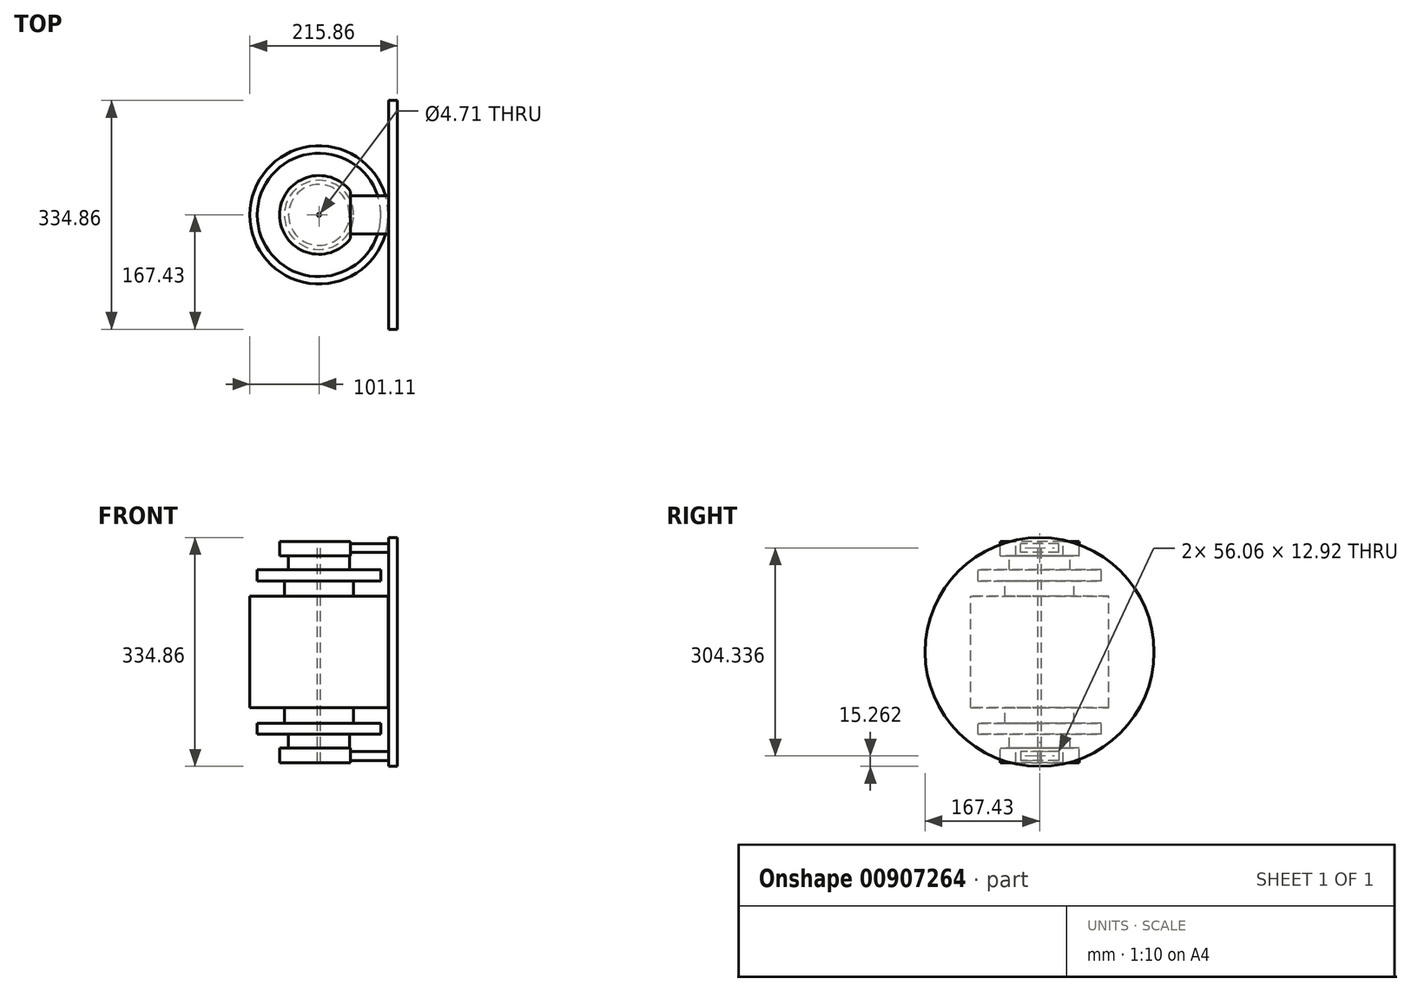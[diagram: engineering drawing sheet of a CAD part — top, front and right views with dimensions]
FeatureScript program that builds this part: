
annotation { "Feature Type Name" : "Feature", "Feature Type Description" : "" }
export const myFeature = defineFeature(function(context is Context, id is Id, definition is map)
    precondition{}
    {
        {
            var Q0;
            Q0=qCreatedBy(makeId("Front.planeOp"),FACE);
            var sketch = newSketch(context, id + "F0", { "sketchPlane" : qUnion([Q0])});
            skLineSegment(sketch, "E0", {"start": v(0, 161.96) * mm, "end": v(0, -142.84) * mm, "construction": true});
            skLineSegment(sketch, "E1", {"start": v(2.35, 161.96) * mm, "end": v(2.35, -142.84) * mm});
            skLineSegment(sketch, "E2", {"start": v(2.35, 161.96) * mm, "end": v(19.28, 161.96) * mm});
            skLineSegment(sketch, "E3", {"start": v(19.28, 161.96) * mm, "end": v(57.62, 161.96) * mm});
            skLineSegment(sketch, "E4", {"start": v(57.62, 161.96) * mm, "end": v(57.62, 140.5) * mm});
            skLineSegment(sketch, "E5", {"start": v(57.62, 140.5) * mm, "end": v(44.53, 140.5) * mm});
            skLineSegment(sketch, "E6", {"start": v(44.53, 140.5) * mm, "end": v(44.53, 120.4) * mm});
            skLineSegment(sketch, "E7", {"start": v(44.53, 120.4) * mm, "end": v(90.35, 120.4) * mm});
            skLineSegment(sketch, "E8", {"start": v(90.35, 120.4) * mm, "end": v(90.35, 104.03) * mm});
            skLineSegment(sketch, "E9", {"start": v(90.35, 104.03) * mm, "end": v(50.6, 104.03) * mm});
            skLineSegment(sketch, "E10", {"start": v(50.6, 104.03) * mm, "end": v(50.6, 81.6) * mm});
            skLineSegment(sketch, "E11", {"start": v(50.6, 81.6) * mm, "end": v(101.1, 81.6) * mm});
            skLineSegment(sketch, "E12", {"start": v(101.1, 81.6) * mm, "end": v(101.1, 0) * mm});
            skLineSegment(sketch, "E13", {"start": v(0, 0) * mm, "end": v(144.55, 0) * mm});
            skLineSegment(sketch, "E14.MirrorCS", {"start": v(101.1, -81.6) * mm, "end": v(101.1, 0) * mm});
            skLineSegment(sketch, "E15.MirrorCS", {"start": v(50.6, -81.6) * mm, "end": v(101.1, -81.6) * mm});
            skLineSegment(sketch, "E16.MirrorCS", {"start": v(50.6, -104.03) * mm, "end": v(50.6, -81.6) * mm});
            skLineSegment(sketch, "E17.MirrorCS", {"start": v(90.35, -104.03) * mm, "end": v(50.6, -104.03) * mm});
            skLineSegment(sketch, "E18.MirrorCS", {"start": v(90.35, -120.4) * mm, "end": v(90.35, -104.03) * mm});
            skLineSegment(sketch, "E19.MirrorCS", {"start": v(44.53, -120.4) * mm, "end": v(90.35, -120.4) * mm});
            skLineSegment(sketch, "E20.MirrorCS", {"start": v(44.53, -140.5) * mm, "end": v(44.53, -120.4) * mm});
            skLineSegment(sketch, "E21.MirrorCS", {"start": v(57.62, -161.96) * mm, "end": v(57.62, -140.5) * mm});
            skLineSegment(sketch, "E22.MirrorCS", {"start": v(19.28, -161.96) * mm, "end": v(57.62, -161.96) * mm});
            skLineSegment(sketch, "E23.MirrorCS", {"start": v(2.35, -161.96) * mm, "end": v(19.28, -161.96) * mm});
            skLineSegment(sketch, "E24", {"start": v(2.35, -142.84) * mm, "end": v(2.35, -161.96) * mm});
            skLineSegment(sketch, "E25", {"start": v(44.53, -140.5) * mm, "end": v(57.62, -140.5) * mm});
            skSolve(sketch);
        }
        {
            var Q0;
            Q0 = qSketchRegion(id + "F0", true);
            var Q1;
            Q1=sQuery(id+"F0.wireOp",EDGE,"E0");
            revolve(context, id + "F1", {"surfaceOperationType" : NewSurfaceOperationType.NEW, "entities" : qUnion([Q0]), "axis" : qUnion([Q1]), "revolveType" : RevolveType.FULL});
        }
        {
            var Q0;
            Q0=qCreatedBy(makeId("Front.planeOp"),FACE);
            var sketch = newSketch(context, id + "F2", { "sketchPlane" : qUnion([Q0])});
            skLineSegment(sketch, "E26.bottom", {"start": v(46.17, 192.82) * mm, "end": v(115.62, 192.82) * mm});
            skLineSegment(sketch, "E26.top", {"start": v(46.17, 133.23) * mm, "end": v(115.62, 133.23) * mm});
            skLineSegment(sketch, "E26.left", {"start": v(46.17, 192.82) * mm, "end": v(46.17, 133.23) * mm});
            skLineSegment(sketch, "E26.right", {"start": v(115.62, 192.82) * mm, "end": v(115.62, 133.23) * mm});
            skLineSegment(sketch, "E27.MirrorCS", {"start": v(115.62, -192.82) * mm, "end": v(115.62, -133.23) * mm});
            skLineSegment(sketch, "E28.MirrorCS", {"start": v(46.17, -133.23) * mm, "end": v(115.62, -133.23) * mm});
            skLineSegment(sketch, "E29.MirrorCS", {"start": v(46.17, -192.82) * mm, "end": v(115.62, -192.82) * mm});
            skLineSegment(sketch, "E30.MirrorCS", {"start": v(46.17, -192.82) * mm, "end": v(46.17, -133.23) * mm});
            skSolve(sketch);
        }
        {
            var Q0;
            Q0 = qSketchRegion(id + "F2", true);
            extrude(context, id + "F3", {"entities" : qUnion([Q0]), "operationType" : NewBodyOperationType.REMOVE, "endBound" : BoundingType.SYMMETRIC, "oppositeDirection" : true, "depth" : 254 * mm, "offsetDistance" : 25.4 * mm});
        }
        {
            var Q0;
            Q0=makeQuery(id+"F3.boolean.opBoolean","COPY",FACE,{"derivedFrom":makeQuery(id+"F3.opExtrude","SWEPT_FACE",FACE,{"disambiguationData":[OSD([sQuery(id+"F2.wireOp",EDGE,"E26.left")])]})});
            var sketch = newSketch(context, id + "F4", { "sketchPlane" : qUnion([Q0])});
            skLineSegment(sketch, "E31.bottom", {"start": v(28.03, 145.7) * mm, "end": v(-28.03, 145.7) * mm});
            skLineSegment(sketch, "E31.top", {"start": v(28.03, 158.63) * mm, "end": v(-28.03, 158.63) * mm});
            skLineSegment(sketch, "E31.left", {"start": v(28.03, 145.7) * mm, "end": v(28.03, 158.63) * mm});
            skLineSegment(sketch, "E31.right", {"start": v(-28.03, 145.7) * mm, "end": v(-28.03, 158.63) * mm});
            skPoint(sketch, "E31.middle", {"position": v(0, 152.17) * mm});
            skLineSegment(sketch, "E32.MirrorCS", {"start": v(28.03, -145.7) * mm, "end": v(-28.03, -145.7) * mm});
            skLineSegment(sketch, "E33.MirrorCS", {"start": v(28.03, -145.7) * mm, "end": v(28.03, -158.63) * mm});
            skLineSegment(sketch, "E34.MirrorCS", {"start": v(28.03, -158.63) * mm, "end": v(-28.03, -158.63) * mm});
            skLineSegment(sketch, "E35.MirrorCS", {"start": v(-28.03, -145.7) * mm, "end": v(-28.03, -158.63) * mm});
            skSolve(sketch);
        }
        {
            var Q0;
            Q0 = qSketchRegion(id + "F4", true);
            extrude(context, id + "F5", {"entities" : qUnion([Q0]), "operationType" : NewBodyOperationType.ADD, "depth" : 55.88 * mm, "offsetDistance" : 25.4 * mm});
        }
        {
            var Q0;
            Q0=makeQuery(id+"F5.opExtrude","CAP_FACE",FACE,{"disambiguationData":[OSD([sQuery(id+"F4.wireOp",EDGE,"E31.bottom"),sQuery(id+"F4.wireOp",EDGE,"E31.top"),sQuery(id+"F4.wireOp",EDGE,"E31.left"),sQuery(id+"F4.wireOp",EDGE,"E31.right")])],"isStart":false});
            var sketch = newSketch(context, id + "F6", { "sketchPlane" : qUnion([Q0])});
            skCircle(sketch, "E36", {"center": v(0, 0) * mm, "radius": 167.43 * mm});
            skSolve(sketch);
        }
        {
            var Q0;
            Q0 = qSketchRegion(id + "F6", true);
            extrude(context, id + "F7", {"entities" : qUnion([Q0]), "operationType" : NewBodyOperationType.ADD, "depth" : 12.7 * mm, "offsetDistance" : 25.4 * mm});
        }
    });
